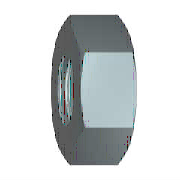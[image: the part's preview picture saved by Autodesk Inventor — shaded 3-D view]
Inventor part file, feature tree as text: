
AUTODESK INVENTOR PART (.ipt)
format: ipt  version: 2024.3 (Build 283343000, 343)  size: 162,304 bytes
history: native  units: mm (DEFAULTED — no unit token found)
features: chamfer x1, hole x1, other x1, plane x1
ambient origin geometry x7: Origin, YZ Plane, XZ Plane, X Axis, Y Axis, Z Axis, Center Point
bodies: Solid1 (feature_tree), Body (feature_tree)
feature tree (4):
  chamfer  "Chamfer1"  Distance=4.618802mm
  hole  "Thread"  [1 undecoded]
  other  "Work Axis1"
  plane  "Work Plane1"
note: 1 required parameter value undecoded (feature->parameter linkage not recoverable at this tier; creation-order binding heuristic only, values carry confidence <= 0.55)
